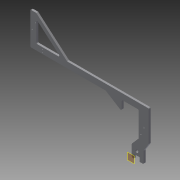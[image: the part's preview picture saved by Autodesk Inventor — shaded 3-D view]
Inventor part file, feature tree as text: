
AUTODESK INVENTOR PART (.ipt)
format: ipt  version: 2013 (Build 170138000, 138)  size: 229,888 bytes
history: native  units: in
note: dims shown in document units (in); Inventor stores cm internally (conversion verified against a paired STEP export)
features: extrude x5, sketch x4, fillet x3, plane x2
ambient origin geometry x8: Origin, YZ Plane, XZ Plane, XY Plane, X Axis, Y Axis, Z Axis, Center Point
feature tree (14):
  plane  "Work Plane4"
  plane  "Work Plane3"
  extrude  "Extrusion9"  Depth=1.25in
  extrude  "Extrusion10"  Depth=2.0in
  extrude  "Extrusion11"  Depth=0.75in
  fillet  "Fillet8"  Radius=1.5in
  fillet  "Fillet9"  [1 undecoded]
  extrude  "Extrusion12"  Depth=0.875in
  extrude  "Extrusion13"  TaperAngle=0.0deg  [1 undecoded]
  fillet  "Fillet10"  Radius=6.625in
  sketch  "Sketch8"  dims[d0=0.25in d1=0.5in d2=0.75in d3=0.25in d4=0.5in d5=0.3765in d6=0.5in d8=14.875in d17=4.0833in d19=0.375in d25=1.25in]
  sketch  "Sketch9"  dims[d26=0.125in d27=2.0in]
  sketch  "Sketch10"  dims[d28=1.0in d29=1.0in d30=0.75in d63=1.5in d68=0.0in]
  sketch  "Sketch11"  dims[d69=2.15in d71=0.875in d72=0.0in d73=6.625in d74=3.125in d75=3.0833in d76=9.475in d87=0.25in d88=1.5in d89=1.0in d91=1.0in d93=0.2797in d94=0.5in d95=0.75in d97=0.2797in d98=10.5406in d99=0.25in d100=0.0in d101=0.15in d102=0.15in d103=0.6355in d104=1.113in d105=0.2375in d106=2.019in d107=0.25in d108=0.0in d109=0.125in d110=0.125in d111=1.5in d112=1.5in d113=0.25in d114=0.25in d115=0.125in d116=0.125in d117=1.5in d118=1.5in d119=0.1875in d121=0.25in d122=0.0in d123=0.125in d124=0.3125in d125=0.125in d126=1.5in d127=0.15in d128=0.15in d129=0.398in d130=0.906in d131=0.237in d132=0.125in d133=0.25in d134=0.0in d135=1.0in d136=1.0in d137=0.25in d139=0.25in d140=1.0in d141=0.0in d142=0.125in]
note: 2 required parameter values undecoded (feature->parameter linkage not recoverable at this tier; creation-order binding heuristic only, values carry confidence <= 0.55)
